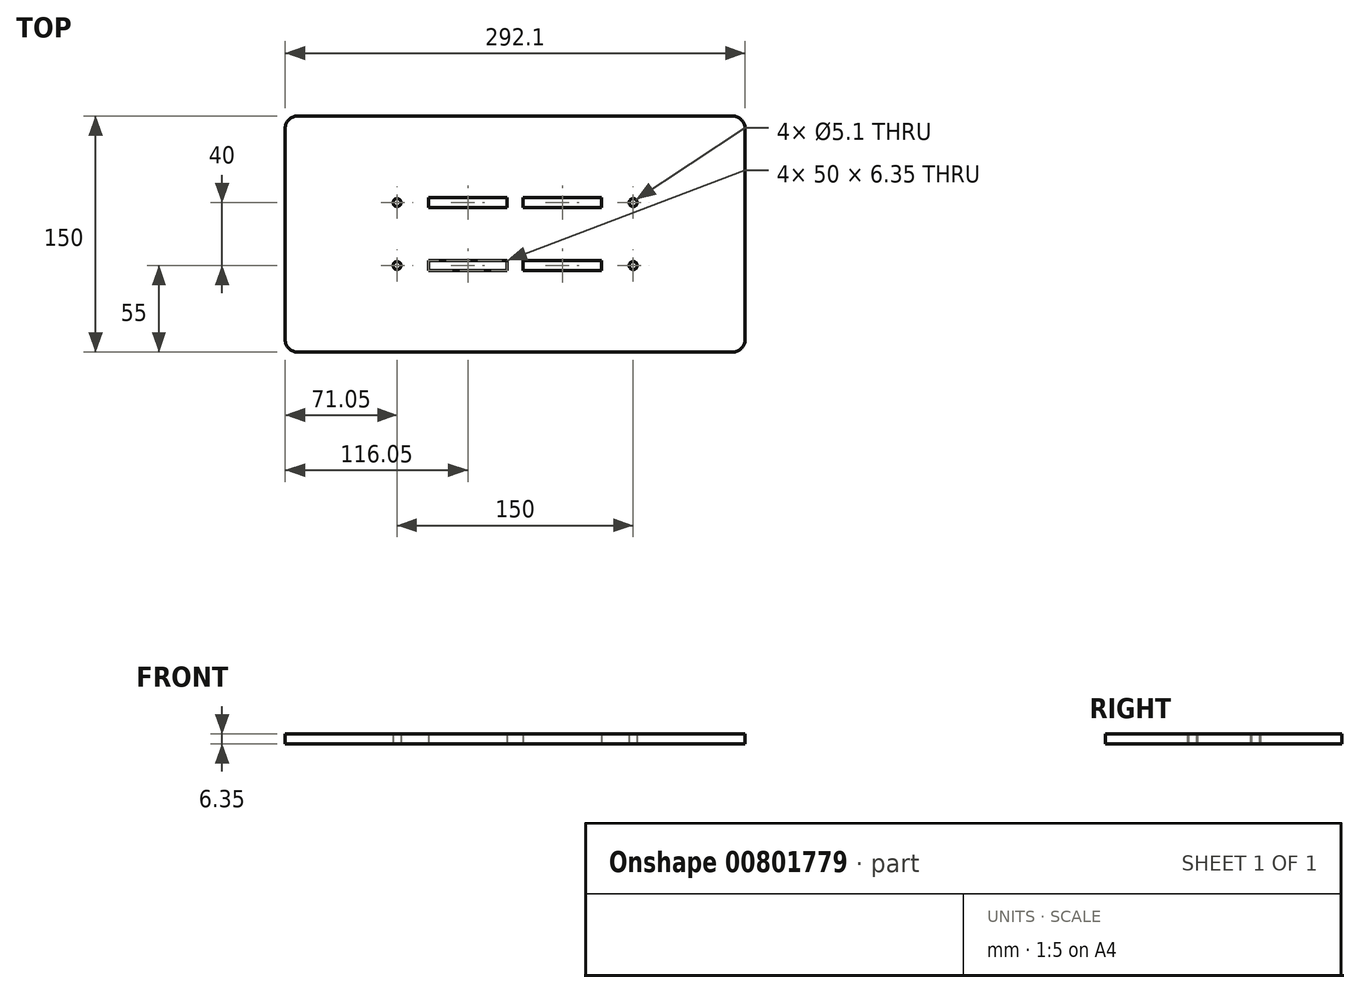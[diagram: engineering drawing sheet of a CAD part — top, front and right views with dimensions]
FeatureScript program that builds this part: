
annotation { "Feature Type Name" : "Feature", "Feature Type Description" : "" }
export const myFeature = defineFeature(function(context is Context, id is Id, definition is map)
    precondition{}
    {
        {
            var Q0;
            Q0=qCreatedBy(makeId("Top.planeOp"),FACE);
            var sketch = newSketch(context, id + "F0", { "sketchPlane" : qUnion([Q0])});
            skLineSegment(sketch, "E0.bottom", {"start": v(75, 20) * mm, "end": v(-75, 20) * mm, "construction": true});
            skLineSegment(sketch, "E0.top", {"start": v(75, -20) * mm, "end": v(-75, -20) * mm, "construction": true});
            skLineSegment(sketch, "E0.left", {"start": v(75, 20) * mm, "end": v(75, -20) * mm, "construction": true});
            skLineSegment(sketch, "E0.right", {"start": v(-75, 20) * mm, "end": v(-75, -20) * mm, "construction": true});
            skPoint(sketch, "E0.middle", {"position": v(0, 0) * mm});
            skCircle(sketch, "E1", {"center": v(-75, 20) * mm, "radius": 2.55 * mm});
            skCircle(sketch, "E2", {"center": v(75, 20) * mm, "radius": 2.55 * mm});
            skCircle(sketch, "E3", {"center": v(75, -20) * mm, "radius": 2.55 * mm});
            skCircle(sketch, "E4", {"center": v(-75, -20) * mm, "radius": 2.55 * mm});
            skLineSegment(sketch, "E5.bottom", {"start": v(-5, 23.18) * mm, "end": v(-55, 23.17) * mm});
            skLineSegment(sketch, "E5.top", {"start": v(-5, 16.82) * mm, "end": v(-55, 16.82) * mm});
            skLineSegment(sketch, "E5.left", {"start": v(-5, 23.18) * mm, "end": v(-5, 16.82) * mm});
            skLineSegment(sketch, "E5.right", {"start": v(-55, 23.18) * mm, "end": v(-55, 16.82) * mm});
            skPoint(sketch, "E5.middle", {"position": v(-30, 20) * mm});
            skLineSegment(sketch, "E6.MirrorCS", {"start": v(5, 23.18) * mm, "end": v(5, 16.82) * mm});
            skLineSegment(sketch, "E7.MirrorCS", {"start": v(55, 23.18) * mm, "end": v(55, 16.82) * mm});
            skLineSegment(sketch, "E8.MirrorCS", {"start": v(5, 23.18) * mm, "end": v(55, 23.18) * mm});
            skLineSegment(sketch, "E9.MirrorCS", {"start": v(5, 16.82) * mm, "end": v(55, 16.83) * mm});
            skPoint(sketch, "E10.MirrorP", {"position": v(30, 20) * mm});
            skLineSegment(sketch, "E11.MirrorCS", {"start": v(5, -23.18) * mm, "end": v(5, -16.82) * mm});
            skLineSegment(sketch, "E12.MirrorCS", {"start": v(55, -23.18) * mm, "end": v(55, -16.82) * mm});
            skLineSegment(sketch, "E13.MirrorCS", {"start": v(-55, -23.18) * mm, "end": v(-55, -16.82) * mm});
            skLineSegment(sketch, "E14.MirrorCS", {"start": v(-5, -23.18) * mm, "end": v(-5, -16.82) * mm});
            skLineSegment(sketch, "E15.MirrorCS", {"start": v(5, -16.82) * mm, "end": v(55, -16.82) * mm});
            skLineSegment(sketch, "E16.MirrorCS", {"start": v(5, -23.18) * mm, "end": v(55, -23.17) * mm});
            skPoint(sketch, "E17.MirrorP", {"position": v(30, -20) * mm});
            skPoint(sketch, "E18.MirrorP", {"position": v(-30, -20) * mm});
            skLineSegment(sketch, "E19.MirrorCS", {"start": v(-5, -23.18) * mm, "end": v(-55, -23.18) * mm});
            skLineSegment(sketch, "E20.MirrorCS", {"start": v(-5, -16.82) * mm, "end": v(-55, -16.82) * mm});
            skLineSegment(sketch, "E21.bottom", {"start": v(138.05, 75) * mm, "end": v(-138.05, 75) * mm});
            skLineSegment(sketch, "E21.top", {"start": v(138.05, -75) * mm, "end": v(-138.05, -75) * mm});
            skLineSegment(sketch, "E21.left", {"start": v(146.05, 67) * mm, "end": v(146.05, -67) * mm});
            skLineSegment(sketch, "E21.right", {"start": v(-146.05, 67) * mm, "end": v(-146.05, -67) * mm});
            skPoint(sketch, "E22.visualSharp", {"position": v(-146.05, 75) * mm});
            skArc(sketch, "E22.filletArc", {"start": v(-138.05, 75) * mm, "mid": v(-143.7, 72.66) * mm, "end": v(-146.05, 67) * mm});
            skPoint(sketch, "E23.visualSharp", {"position": v(-146.05, -75) * mm});
            skArc(sketch, "E23.filletArc", {"start": v(-146.05, -67) * mm, "mid": v(-143.7, -72.66) * mm, "end": v(-138.05, -75) * mm});
            skPoint(sketch, "E24.visualSharp", {"position": v(146.05, -75) * mm});
            skArc(sketch, "E24.filletArc", {"start": v(138.05, -75) * mm, "mid": v(143.7, -72.66) * mm, "end": v(146.05, -67) * mm});
            skPoint(sketch, "E25.visualSharp", {"position": v(146.05, 75) * mm});
            skArc(sketch, "E25.filletArc", {"start": v(146.05, 67) * mm, "mid": v(143.7, 72.66) * mm, "end": v(138.05, 75) * mm});
            skSolve(sketch);
        }
        {
            var Q0;
            Q0=makeQuery(id+"F0.imprint","IMPRINT",FACE,{"disambiguationData":[TD([[makeQuery(id+"F0.imprint","IMPRINT",EDGE,{"derivedFrom":sQuery(id+"F0.wireOp",EDGE,"E1")}),-1.0]])]});
            extrude(context, id + "F1", {"entities" : qUnion([Q0]), "depth" : 6.35 * mm, "offsetDistance" : 25 * mm});
        }
    });
